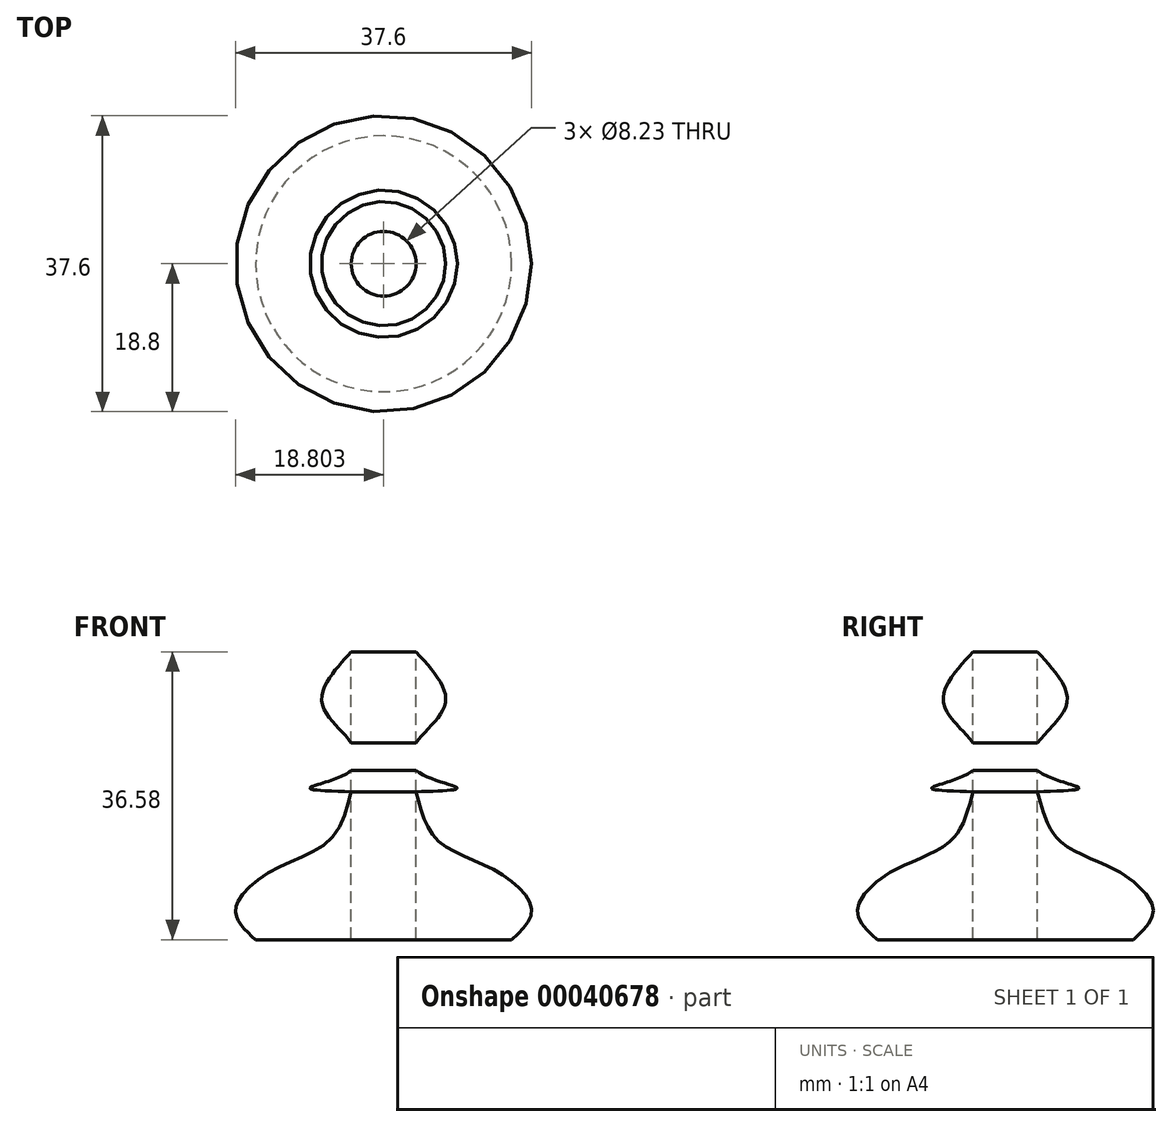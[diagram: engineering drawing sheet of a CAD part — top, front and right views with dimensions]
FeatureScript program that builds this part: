
annotation { "Feature Type Name" : "Feature", "Feature Type Description" : "" }
export const myFeature = defineFeature(function(context is Context, id is Id, definition is map)
    precondition{}
    {
        {
            var Q0;
            Q0=qCreatedBy(makeId("Front.planeOp"),FACE);
            var sketch = newSketch(context, id + "F0", { "sketchPlane" : qUnion([Q0])});
            skFitSpline(sketch, "E0", {"points": [v(0, 45.3) * mm, v(-3.74, 38.88) * mm, v(0, 33.7) * mm, v(0, 30.24) * mm, v(-5.22, 28.02) * mm, v(0, 27.53) * mm], "startDerivative": vector(-26.28, -28.73) * mm, "endDerivative": vector(42.4, -1.13) * mm});
            skLineSegment(sketch, "E1", {"start": v(0, 27.53) * mm, "end": v(0, 21.36) * mm});
            skLineSegment(sketch, "E2", {"start": v(0, 45.3) * mm, "end": v(0, 8.78) * mm});
            skFitSpline(sketch, "E3", {"points": [v(0, 27.53) * mm, v(-2.75, 21.36) * mm, v(-10.38, 17.33) * mm, v(-14.69, 12.44) * mm, v(-12.14, 8.72) * mm], "startDerivative": vector(-6.7, -27.29) * mm, "endDerivative": vector(18.6, -16.98) * mm});
            skLineSegment(sketch, "E4", {"start": v(-12.14, 8.72) * mm, "end": v(0, 8.78) * mm});
            skLineSegment(sketch, "E5", {"start": v(4.11, 45.3) * mm, "end": v(4.11, 8.78) * mm});
            skFitSpline(sketch, "E6", {"points": [v(0, 32) * mm, v(0, 31.88) * mm], "startDerivative": vector(0, -0.13) * mm, "endDerivative": vector(0, -0.13) * mm});
            skFitSpline(sketch, "E7", {"points": [v(0, 45.3) * mm, v(1.5, 50.7) * mm], "startDerivative": vector(1.5, 5.4) * mm, "endDerivative": vector(1.5, 5.4) * mm});
            skSolve(sketch);
        }
        {
            var Q0;
            {var subQ2=sQuery(id+"F0.wireOp",EDGE,"E3");Q0=makeQuery(id+"F0.imprint","IMPRINT",FACE,{"disambiguationData":[TD([[makeQuery(id+"F0.imprint","IMPRINT",EDGE,{"derivedFrom":subQ2}),1.0]])]});}
            var Q1;
            {var subQ0=sQuery(id+"F0.wireOp",EDGE,"E2");var subQ1=sQuery(id+"F0.wireOp",EDGE,"E0");var subQ2=makeQuery(id+"F0.imprint","INTERSECT",VERTEX,{"disambiguationData":[OD(2.0)],"derivedFrom":[subQ1,subQ0]});Q1=makeQuery(id+"F0.imprint","IMPRINT",FACE,{"disambiguationData":[TD([[makeQuery(id+"F0.imprint","IMPRINT",EDGE,{"disambiguationData":[TD([[subQ2,-1.0]])],"derivedFrom":subQ1}),1.0]])]});}
            var Q2;
            {var subQ0=sQuery(id+"F0.wireOp",EDGE,"E2");var subQ1=sQuery(id+"F0.wireOp",EDGE,"E0");var subQ3=makeQuery(id+"F0.imprint","INTERSECT",VERTEX,{"disambiguationData":[OD(0.0)],"derivedFrom":[subQ1,subQ0]});Q2=makeQuery(id+"F0.imprint","IMPRINT",FACE,{"disambiguationData":[TD([[makeQuery(id+"F0.imprint","IMPRINT",EDGE,{"disambiguationData":[TD([[subQ3,-1.0]])],"derivedFrom":subQ1}),1.0]])]});}
            var Q3;
            Q3=sQuery(id+"F0.wireOp",EDGE,"E5");
            revolve(context, id + "F1", {"entities" : qUnion([Q0, Q1, Q2]), "axis" : qUnion([Q3]), "revolveType" : RevolveType.FULL});
        }
    });
